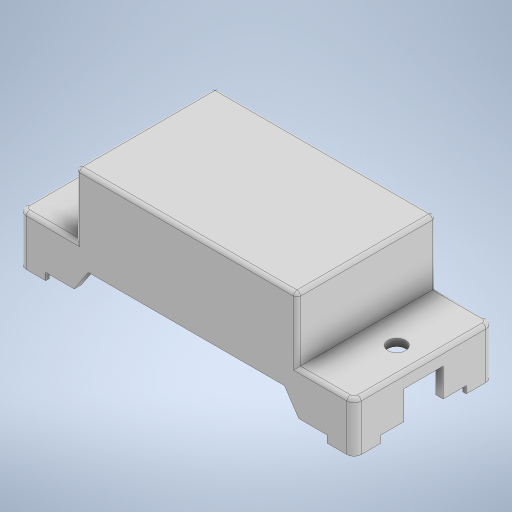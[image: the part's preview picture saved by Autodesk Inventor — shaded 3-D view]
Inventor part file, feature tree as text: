
AUTODESK INVENTOR PART (.ipt)
format: ipt  version: 2024 (Build 280153000, 153)  size: 412,160 bytes
history: native  units: in
note: dims shown in document units (in); Inventor stores cm internally (conversion verified against a paired STEP export)
features: extrude x8, sketch x8, chamfer x4, fillet x2, mirror x1
ambient origin geometry x8: Origin, YZ Plane, XZ Plane, XY Plane, X Axis, Y Axis, Z Axis, Center Point
bodies: Solid1 (feature_tree)
feature tree (23):
  extrude  "Extrusion1"  Depth=1.95in
  extrude  "Extrusion2"  Depth=1.6in TaperAngle=0.0deg
  extrude  "Extrusion3"  Depth=0.8in
  extrude  "Extrusion4"  Depth=1.95in
  extrude  "Extrusion5"  Depth=3.1in
  extrude  "Extrusion6"  Depth=0.9in
  extrude  "Extrusion7"  Depth=0.25in
  extrude  "Extrusion8"  Depth=0.1in
  mirror  "Mirror1"
  fillet  "Fillet1"  Radius=0.1in
  fillet  "Fillet2"  Radius=0.1in
  chamfer  "Chamfer1"  Distance=0.1in
  chamfer  "Chamfer2"  Distance=2.35in
  chamfer  "Chamfer3"  Distance=0.6in
  chamfer  "Chamfer4"  Distance=2.9in
  sketch  "Sketch1"  dims[d0=4.7in d1=1.95in]
  sketch  "Sketch2"  dims[d2=0.975in d3=1.6in d4=0.0in]
  sketch  "Sketch3"  dims[d5=3.05in d6=0.8in]
  sketch  "Sketch4"  dims[d7=0.8in d8=1.95in]
  sketch  "Sketch5"  dims[d9=1.95in d10=3.1in]
  sketch  "Sketch6"  dims[d11=0.9in d12=0.0in d13=0.25in]
  sketch  "Sketch7"  dims[d14=0.25in d15=0.25in]
  sketch  "Sketch8"  dims[d16=0.9in d17=0.0in d18=0.1in d19=0.1in d20=0.1in d21=0.1in d22=2.35in d23=0.6in d24=0.0in d25=2.9in d26=0.9in d27=0.0in d28=0.05in d29=0.05in d30=3.95in d31=1.975in d32=1.2in d33=0.6in d34=1.2in d35=0.6in d38=0.1in d39=0.0in d40=3.95in d41=1.975in d42=2.75in d43=1.375in d44=2.75in d45=1.375in d46=0.3in d47=0.0in d48=0.55in d49=0.275in d50=0.4in d51=0.0in d52=0.1in d53=0.05in d54=0.2in d55=0.3in d56=45.0deg d57=0.2in d58=0.3in d59=45.0deg d60=0.2in d61=0.3in d62=45.0deg d63=0.2in d64=0.3in d65=45.0deg]
